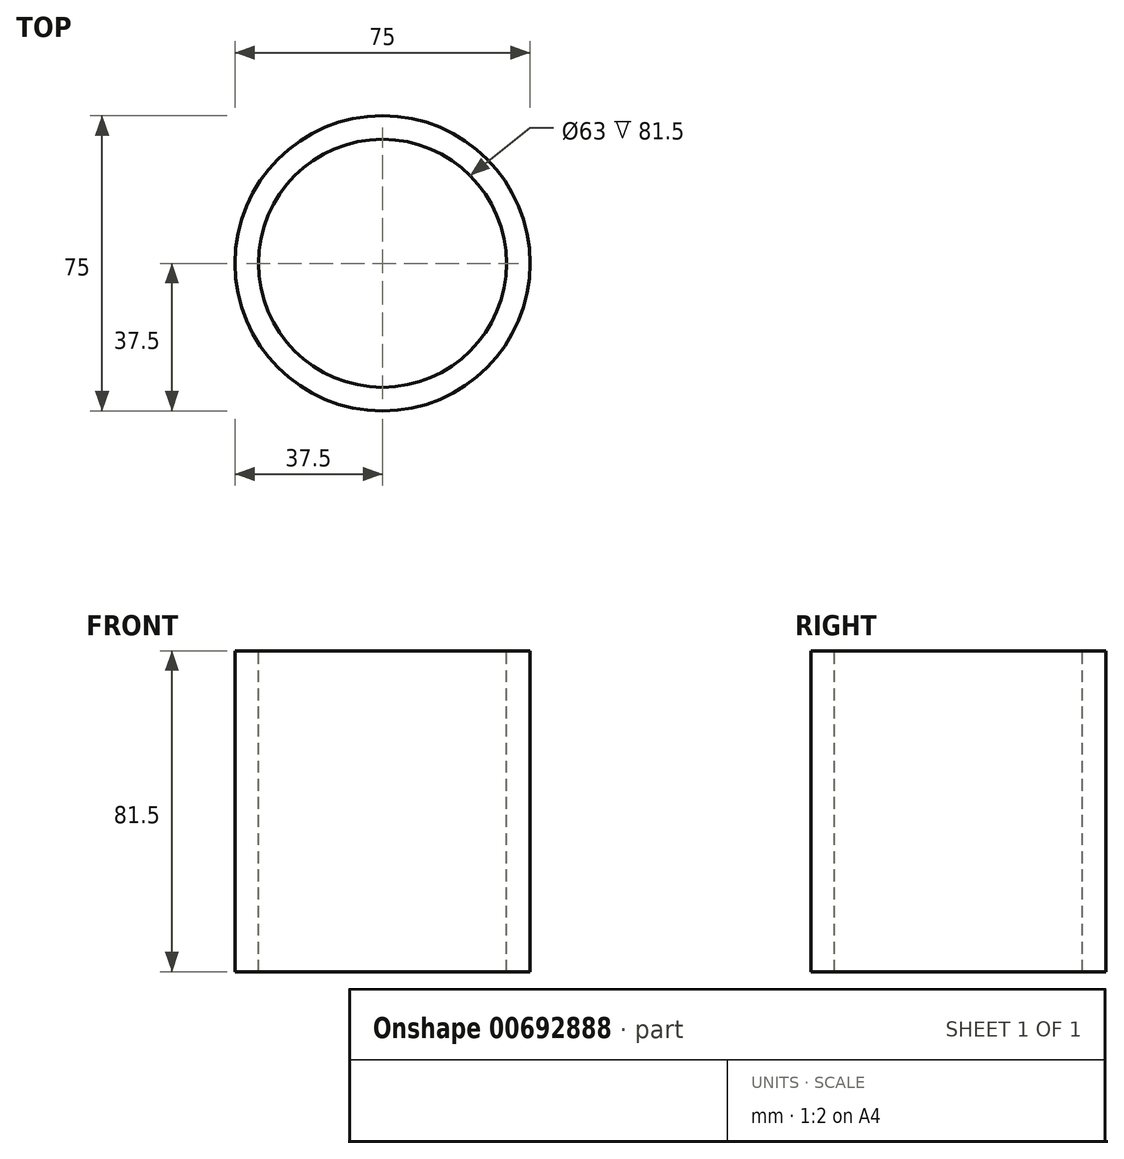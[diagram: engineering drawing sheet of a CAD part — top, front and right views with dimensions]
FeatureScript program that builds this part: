
annotation { "Feature Type Name" : "Feature", "Feature Type Description" : "" }
export const myFeature = defineFeature(function(context is Context, id is Id, definition is map)
    precondition{}
    {
        {
            var Q0;
            Q0=qCreatedBy(makeId("Front.planeOp"),FACE);
            var sketch = newSketch(context, id + "F0", { "sketchPlane" : qUnion([Q0])});
            skLineSegment(sketch, "E0", {"start": v(-37.5, 0) * mm, "end": v(-37.5, 81.5) * mm});
            skLineSegment(sketch, "E1", {"start": v(-37.5, 81.5) * mm, "end": v(-31.5, 81.5) * mm});
            skLineSegment(sketch, "E2", {"start": v(-31.5, 81.5) * mm, "end": v(-31.5, 42.5) * mm});
            skLineSegment(sketch, "E3", {"start": v(-31.5, 42.5) * mm, "end": v(-31.5, 0) * mm});
            skLineSegment(sketch, "E4", {"start": v(-31.5, 0) * mm, "end": v(-37.5, 0) * mm});
            skLineSegment(sketch, "E5", {"start": v(0, 0) * mm, "end": v(0, -22.63) * mm});
            skSolve(sketch);
        }
        {
            var Q0;
            Q0=makeQuery(id+"F0.imprint","IMPRINT",FACE,{"disambiguationData":[TD([[makeQuery(id+"F0.imprint","IMPRINT",EDGE,{"derivedFrom":sQuery(id+"F0.wireOp",EDGE,"E0")}),-1.0]])]});
            var Q1;
            Q1=sQuery(id+"F0.wireOp",EDGE,"E5");
            revolve(context, id + "F1", {"entities" : qUnion([Q0]), "axis" : qUnion([Q1]), "revolveType" : RevolveType.FULL});
        }
    });
